# Revit family: MCC_Concrete-Rectangular-Column
name_source: partatom
category: Structural Columns
revit_build: Autodesk Revit 2014 (Build: 20131024_2115(x64)
units: mm (PartAtom-declared; Revit-internal decimal feet)

## types (17) — shared parameters

## per-type parameters (varying)
| type | Column Length | Column Width |
| 38x50 COL | 2' - 0" | 3' - 0" |
| 32x36 COL | 3' - 0" | 2' - 8" |
| 24x28 COL | 2' - 4" | 2' - 0" |
| 20x48 COL | 4' - 0" | 1' - 8" |
| 32x56 COL | 4' - 8" | 2' - 8" |
| 36x48 COL | 4' - 0" | 3' - 0" |
| 18x24 COL | 1' - 6" | 2' - 0" |
| 24x42 COL | 3' - 6" | 2' - 0" |
| 26x32 COL | 2' - 8" | 2' - 2" |
| 18x30 COL | 2' - 6" | 1' - 6" |
| 30x42 COL | 3' - 6" | 2' - 6" |
| 24x48 COL | 4' - 0" | 2' - 0" |
| 12x40 COL | 3' - 4" | 1' - 0" |
| 16x48 COL | 4' - 0" | 1' - 4" |
| 32x50 Col. | 4' - 2" | 2' - 8" |
| 44x56 Col | 4' - 8" | 3' - 8" |
| 26x38 COL | 2' - 2" | 3' - 2" |

## geometry (parser evidence)
native form markers: Sweep x3
no freeform markers — native parametric forms only
